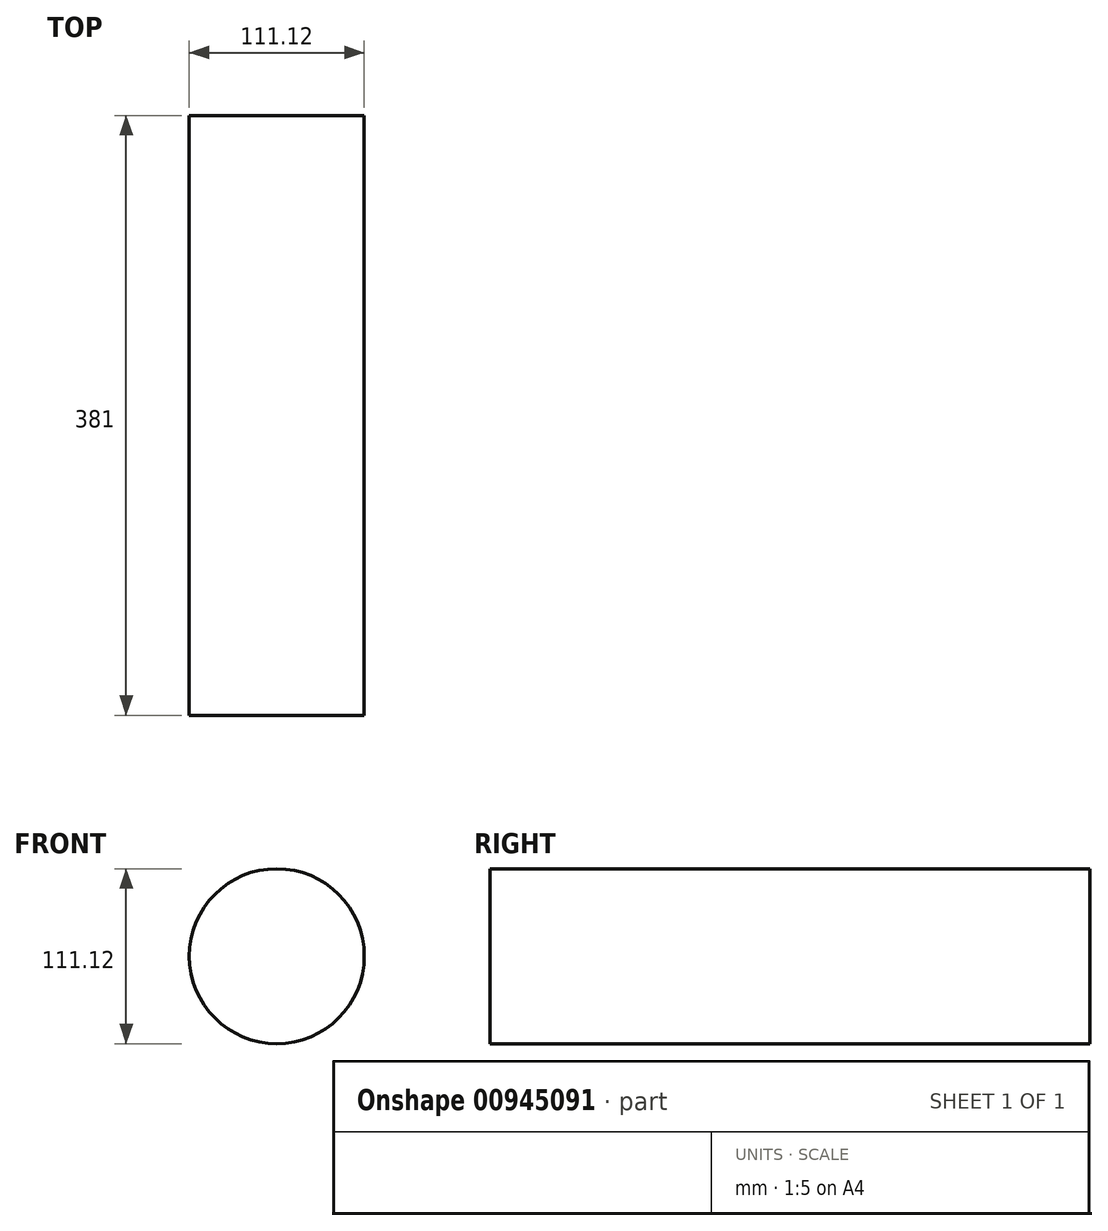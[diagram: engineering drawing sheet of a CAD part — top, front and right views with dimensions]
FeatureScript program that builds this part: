
annotation { "Feature Type Name" : "Feature", "Feature Type Description" : "" }
export const myFeature = defineFeature(function(context is Context, id is Id, definition is map)
    precondition{}
    {
        {
            var Q0;
            Q0=qCreatedBy(makeId("Front.planeOp"),FACE);
            var sketch = newSketch(context, id + "F0", { "sketchPlane" : qUnion([Q0])});
            skCircle(sketch, "E0", {"center": v(0, 0) * mm, "radius": 55.56 * mm});
            skSolve(sketch);
        }
        {
            var Q0;
            Q0 = qSketchRegion(id + "F0", true);
            extrude(context, id + "F1", {"entities" : qUnion([Q0]), "depth" : 381 * mm, "offsetDistance" : 25.4 * mm});
        }
    });
